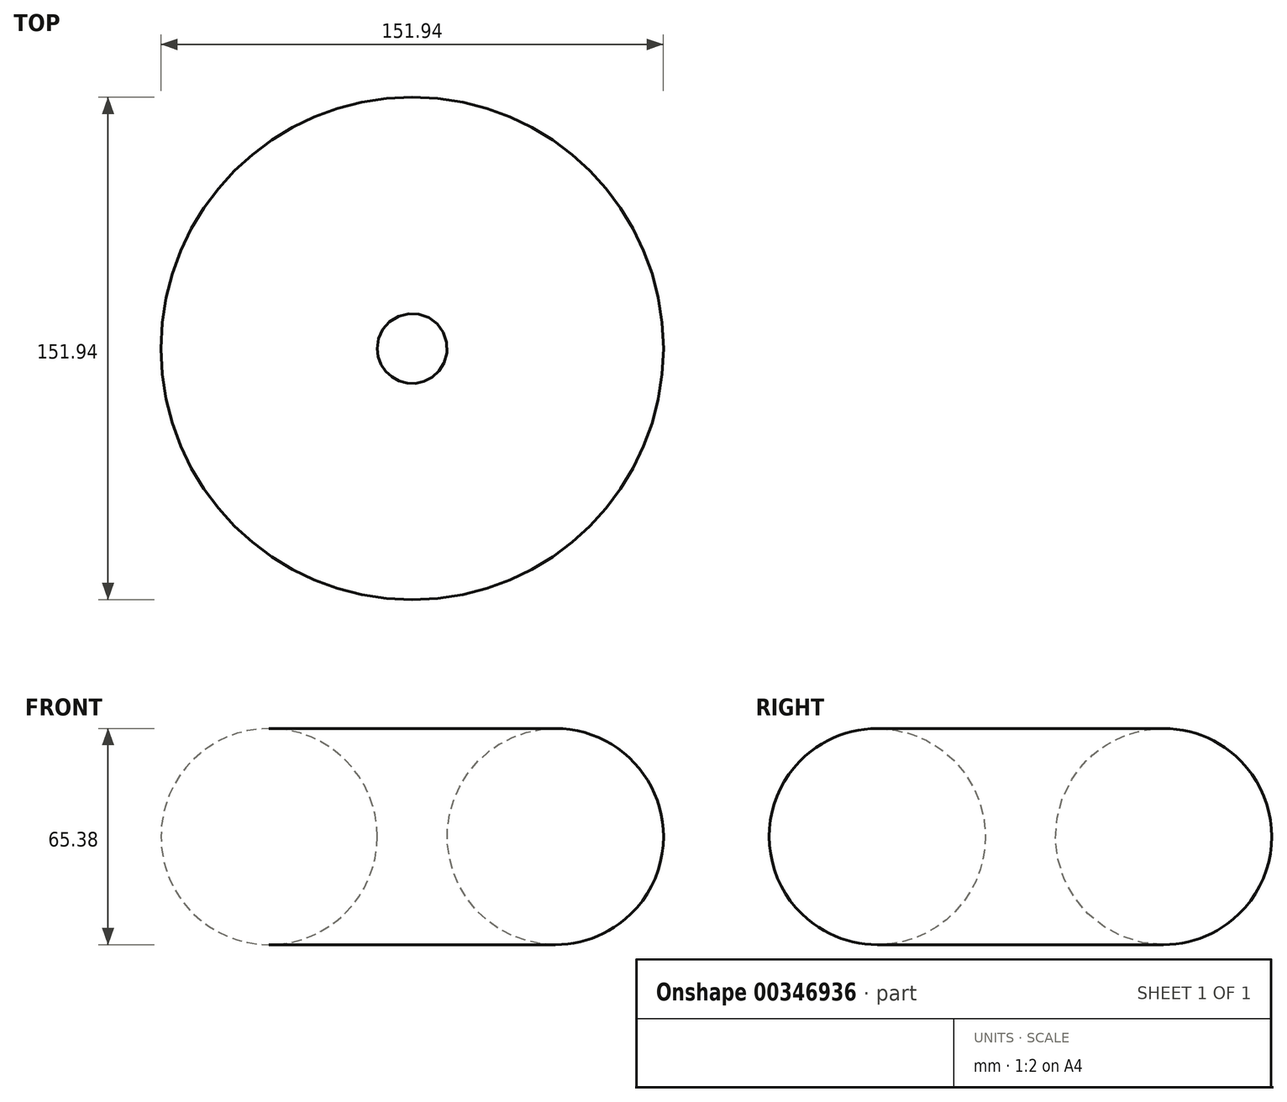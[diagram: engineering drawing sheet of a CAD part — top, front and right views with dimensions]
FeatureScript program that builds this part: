
annotation { "Feature Type Name" : "Feature", "Feature Type Description" : "" }
export const myFeature = defineFeature(function(context is Context, id is Id, definition is map)
    precondition{}
    {
        {
            var Q0;
            Q0=qCreatedBy(makeId("Front.planeOp"),FACE);
            var sketch = newSketch(context, id + "F0", { "sketchPlane" : qUnion([Q0])});
            skCircle(sketch, "E0", {"center": v(43.29, 0) * mm, "radius": 32.69 * mm});
            skLineSegment(sketch, "E1", {"start": v(0, 0) * mm, "end": v(0, 81.7) * mm, "construction": true});
            skSolve(sketch);
        }
        {
            var Q0;
            Q0=makeQuery(id+"F0.imprint","IMPRINT",FACE,{"disambiguationData":[TD([[makeQuery(id+"F0.imprint","IMPRINT",EDGE,{"derivedFrom":sQuery(id+"F0.wireOp",EDGE,"E0")}),1.0]])]});
            var Q1;
            Q1=sQuery(id+"F0.wireOp",EDGE,"E0");
            var Q2;
            Q2=sQuery(id+"F0.wireOp",EDGE,"E1");
            revolve(context, id + "F1", {"entities" : qUnion([Q0]), "surfaceEntities" : qUnion([Q1]), "axis" : qUnion([Q2]), "revolveType" : RevolveType.FULL});
        }
    });
